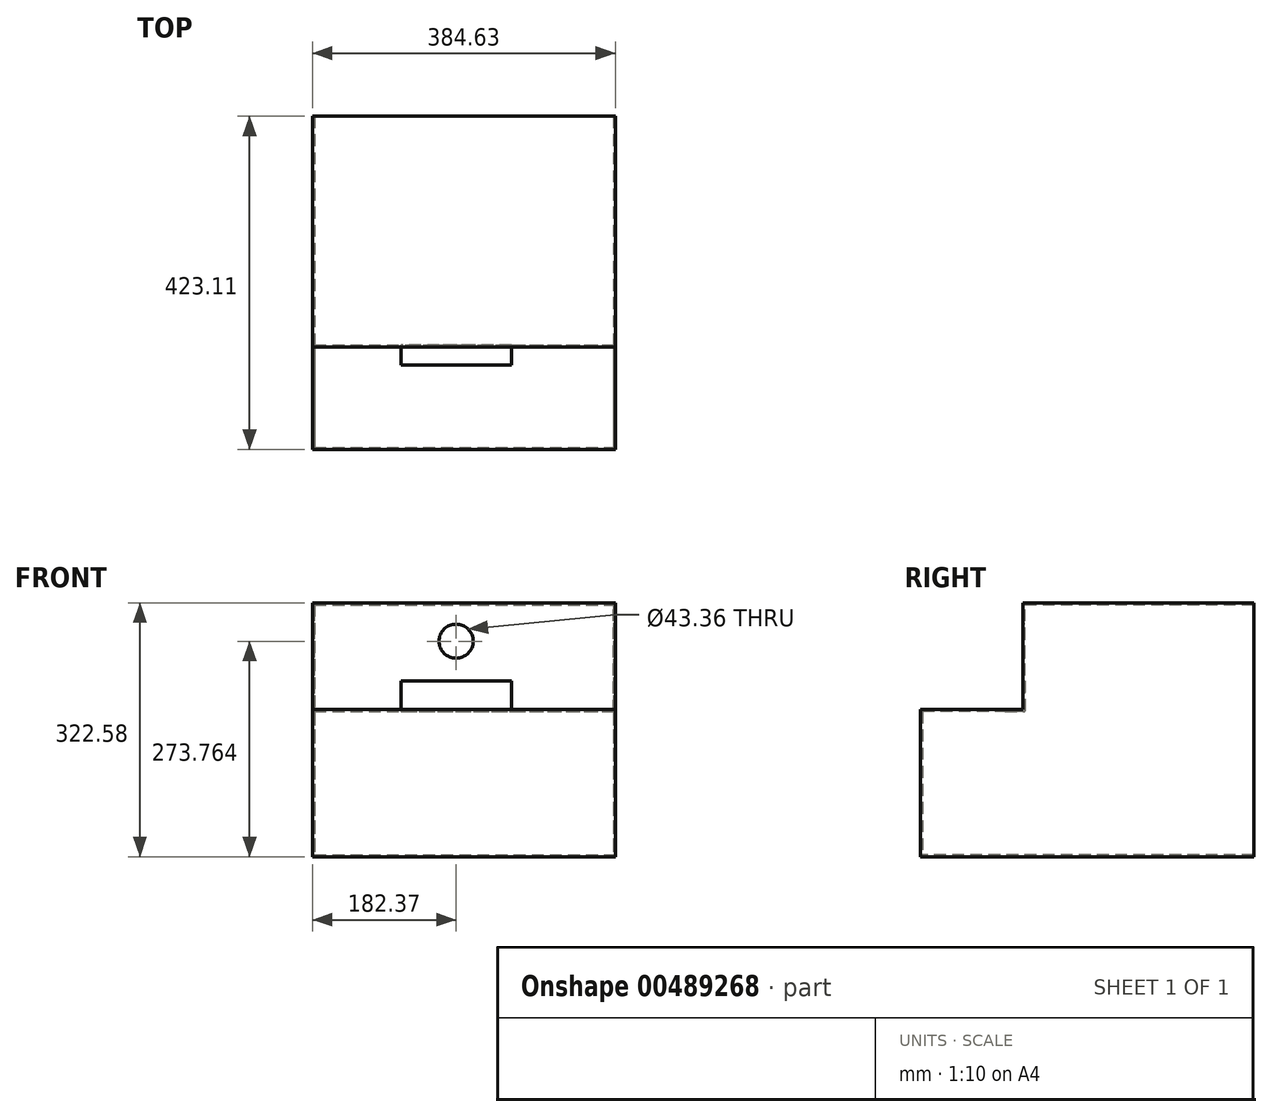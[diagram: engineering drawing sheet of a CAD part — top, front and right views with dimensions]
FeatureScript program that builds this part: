
annotation { "Feature Type Name" : "Feature", "Feature Type Description" : "" }
export const myFeature = defineFeature(function(context is Context, id is Id, definition is map)
    precondition{}
    {
        {
            var Q0;
            Q0=qCreatedBy(makeId("Top.planeOp"),FACE);
            var sketch = newSketch(context, id + "F0", { "sketchPlane" : qUnion([Q0])});
            skLineSegment(sketch, "E0.bottom", {"start": v(-182.37, 134.42) * mm, "end": v(202.26, 134.42) * mm});
            skLineSegment(sketch, "E0.top", {"start": v(-182.37, -129.94) * mm, "end": v(202.26, -129.94) * mm});
            skLineSegment(sketch, "E0.left", {"start": v(-182.37, 134.42) * mm, "end": v(-182.37, -129.94) * mm});
            skLineSegment(sketch, "E0.right", {"start": v(202.26, 134.42) * mm, "end": v(202.26, -129.94) * mm});
            skSolve(sketch);
        }
        {
            var Q0;
            Q0=makeQuery(id+"F0.imprint","IMPRINT",FACE,{"disambiguationData":[TD([[makeQuery(id+"F0.imprint","IMPRINT",EDGE,{"derivedFrom":sQuery(id+"F0.wireOp",EDGE,"E0.bottom")}),-1.0]])]});
            extrude(context, id + "F1", {"entities" : qUnion([Q0]), "depth" : 322.58 * mm});
        }
        {
            var Q0;
            Q0=makeQuery(id+"F1.opExtrude","CAP_FACE",FACE,{"disambiguationData":[OSD([sQuery(id+"F0.wireOp",EDGE,"E0.bottom"),sQuery(id+"F0.wireOp",EDGE,"E0.top"),sQuery(id+"F0.wireOp",EDGE,"E0.left"),sQuery(id+"F0.wireOp",EDGE,"E0.right")])],"isStart":false});
            var sketch = newSketch(context, id + "F2", { "sketchPlane" : qUnion([Q0])});
            skLineSegment(sketch, "E1.bottom", {"start": v(-182.37, 0) * mm, "end": v(202.26, 0) * mm});
            skLineSegment(sketch, "E1.top", {"start": v(-182.37, -129.94) * mm, "end": v(202.26, -129.94) * mm});
            skLineSegment(sketch, "E1.left", {"start": v(-182.37, 0) * mm, "end": v(-182.37, -129.94) * mm});
            skLineSegment(sketch, "E1.right", {"start": v(202.26, 0) * mm, "end": v(202.26, -129.94) * mm});
            skSolve(sketch);
        }
        {
            var Q0;
            Q0 = qSketchRegion(id + "F2", true);
            extrude(context, id + "F3", {"entities" : qUnion([Q0]), "operationType" : NewBodyOperationType.REMOVE, "oppositeDirection" : true, "depth" : 135.64 * mm});
        }
        {
            var Q0;
            Q0=makeQuery(id+"F1.opExtrude","SWEPT_FACE",FACE,{"disambiguationData":[OSD([sQuery(id+"F0.wireOp",EDGE,"E0.bottom")])]});
            extrude(context, id + "F4", {"entities" : qUnion([Q0]), "operationType" : NewBodyOperationType.ADD, "depth" : 158.75 * mm});
        }
        {
            var Q0;
            Q0=makeQuery(id+"F4.opExtrude","CAP_FACE",FACE,{"disambiguationData":[OSD([sQuery(id+"F0.wireOp",EDGE,"E0.bottom")])],"isStart":false});
            shell(context, id + "F5", {"entities" : qUnion([Q0]), "thickness" : 2.54 * mm});
        }
        {
            var Q0;
            Q0=makeQuery(id+"F5.opShell","OFFSET_FACE",FACE,{"disambiguationData":[OSD([sQuery(id+"F2.wireOp",EDGE,"E1.bottom")])]});
            var sketch = newSketch(context, id + "F6", { "sketchPlane" : qUnion([Q0])});
            skLineSegment(sketch, "E2.bottom", {"start": v(-70.4, 223.46) * mm, "end": v(69.85, 223.46) * mm});
            skLineSegment(sketch, "E2.top", {"start": v(-70.4, 184.4) * mm, "end": v(69.85, 184.4) * mm});
            skLineSegment(sketch, "E2.left", {"start": v(-70.4, 223.46) * mm, "end": v(-70.4, 184.4) * mm});
            skLineSegment(sketch, "E2.right", {"start": v(69.85, 223.46) * mm, "end": v(69.85, 184.4) * mm});
            skSolve(sketch);
        }
        {
            var Q0;
            Q0=makeQuery(id+"F6.imprint","IMPRINT",FACE,{"disambiguationData":[TD([[makeQuery(id+"F6.imprint","IMPRINT",EDGE,{"derivedFrom":sQuery(id+"F6.wireOp",EDGE,"E2.bottom")}),-1.0]])]});
            extrude(context, id + "F7", {"entities" : qUnion([Q0]), "operationType" : NewBodyOperationType.REMOVE, "oppositeDirection" : true, "depth" : 25.4 * mm});
        }
        {
            var Q0;
            Q0=makeQuery(id+"F3.boolean.opBoolean","COPY",FACE,{"derivedFrom":makeQuery(id+"F3.opExtrude","SWEPT_FACE",FACE,{"disambiguationData":[OSD([sQuery(id+"F2.wireOp",EDGE,"E1.bottom")])]})});
            var sketch = newSketch(context, id + "F8", { "sketchPlane" : qUnion([Q0])});
            skCircle(sketch, "E3", {"center": v(0, 273.76) * mm, "radius": 21.68 * mm});
            skSolve(sketch);
        }
        {
            var Q0;
            Q0=makeQuery(id+"F8.imprint","IMPRINT",FACE,{"disambiguationData":[TD([[makeQuery(id+"F8.imprint","IMPRINT",EDGE,{"derivedFrom":sQuery(id+"F8.wireOp",EDGE,"E3")}),1.0]])]});
            extrude(context, id + "F9", {"entities" : qUnion([Q0]), "operationType" : NewBodyOperationType.REMOVE, "oppositeDirection" : true, "depth" : 25.4 * mm});
        }
    });
